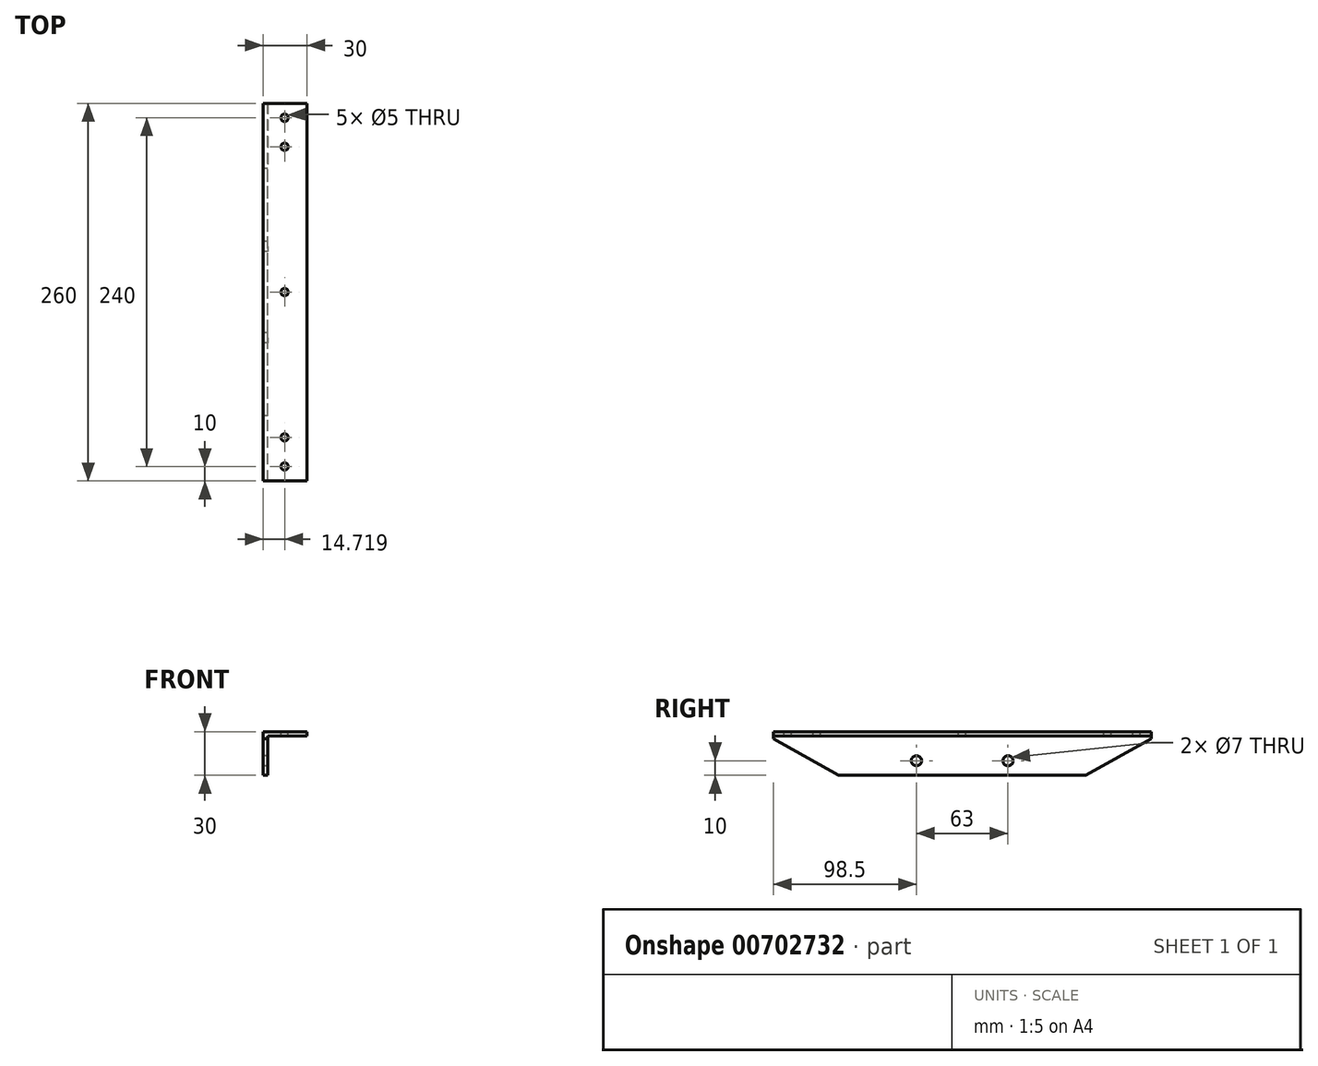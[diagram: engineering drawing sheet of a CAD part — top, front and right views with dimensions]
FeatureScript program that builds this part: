
annotation { "Feature Type Name" : "Feature", "Feature Type Description" : "" }
export const myFeature = defineFeature(function(context is Context, id is Id, definition is map)
    precondition{}
    {
        {
            var Q0;
            Q0=qCreatedBy(makeId("Front.planeOp"),FACE);
            var sketch = newSketch(context, id + "F0", { "sketchPlane" : qUnion([Q0])});
            skLineSegment(sketch, "E0", {"start": v(0, 0) * mm, "end": v(0, 30) * mm});
            skLineSegment(sketch, "E1", {"start": v(0, 30) * mm, "end": v(30, 30) * mm});
            skLineSegment(sketch, "E2", {"start": v(30, 30) * mm, "end": v(30, 27) * mm});
            skLineSegment(sketch, "E3", {"start": v(30, 27) * mm, "end": v(3, 27) * mm});
            skLineSegment(sketch, "E4", {"start": v(3, 27) * mm, "end": v(3, 0) * mm});
            skLineSegment(sketch, "E5", {"start": v(3, 0) * mm, "end": v(0, 0) * mm});
            skSolve(sketch);
        }
        {
            var Q0;
            Q0=makeQuery(id+"F0.imprint","IMPRINT",FACE,{"disambiguationData":[TD([[makeQuery(id+"F0.imprint","IMPRINT",EDGE,{"derivedFrom":sQuery(id+"F0.wireOp",EDGE,"E0")}),-1.0]])]});
            extrude(context, id + "F1", {"entities" : qUnion([Q0]), "endBound" : BoundingType.SYMMETRIC, "depth" : 260 * mm, "offsetDistance" : 25 * mm});
        }
        {
            var Q0;
            Q0=makeQuery(id+"F1.opExtrude","SWEPT_FACE",FACE,{"disambiguationData":[OSD([sQuery(id+"F0.wireOp",EDGE,"E0")])]});
            var sketch = newSketch(context, id + "F2", { "sketchPlane" : qUnion([Q0])});
            skLineSegment(sketch, "E6", {"start": v(0, 30) * mm, "end": v(0, 10) * mm});
            skLineSegment(sketch, "E7", {"start": v(0, 10) * mm, "end": v(-31.5, 10) * mm});
            skLineSegment(sketch, "E8", {"start": v(0, 10) * mm, "end": v(31.5, 10) * mm});
            skSolve(sketch);
        }
        {
            var Q0;
            Q0=sQuery(id+"F2.wireOp",VERTEX,"E7.end");
            var Q1;
            Q1=sQuery(id+"F2.wireOp",VERTEX,"E8.end");
            var Q2;
            Q2=makeQuery(id+"F1.opExtrude","SWEPT_BODY",BODY,{"disambiguationData":[OSD([sQuery(id+"F0.wireOp",EDGE,"E0"),sQuery(id+"F0.wireOp",EDGE,"E1"),sQuery(id+"F0.wireOp",EDGE,"E2"),sQuery(id+"F0.wireOp",EDGE,"E3"),sQuery(id+"F0.wireOp",EDGE,"E4"),sQuery(id+"F0.wireOp",EDGE,"E5")])]});
            hole(context, id + "F3", {"style" : HoleStyle.SIMPLE, "endStyle" : HoleEndStyle.THROUGH, "holeDiameter" : 7 * mm, "majorDiameter" : 5 * mm, "isTappedThrough" : true, "tappedDepth" : 12 * mm, "tapClearance" : 3, "locations" : qUnion([Q0, Q1]), "scope" : qUnion([Q2])});
        }
        {
            var Q0;
            Q0=makeQuery(id+"F1.opExtrude","SWEPT_FACE",FACE,{"disambiguationData":[OSD([sQuery(id+"F0.wireOp",EDGE,"E1")])]});
            var sketch = newSketch(context, id + "F4", { "sketchPlane" : qUnion([Q0])});
            skLineSegment(sketch, "E9", {"start": v(0, 0) * mm, "end": v(14.72, 0) * mm});
            skLineSegment(sketch, "E10", {"start": v(14.72, 0) * mm, "end": v(14.72, 100) * mm});
            skLineSegment(sketch, "E11", {"start": v(14.72, 0) * mm, "end": v(14.72, -100) * mm});
            skLineSegment(sketch, "E12", {"start": v(14.72, -100) * mm, "end": v(14.72, -120) * mm});
            skLineSegment(sketch, "E13", {"start": v(14.72, 100) * mm, "end": v(14.72, 120) * mm});
            skSolve(sketch);
        }
        {
            var Q0;
            Q0=sQuery(id+"F4.wireOp",VERTEX,"1tQewzAj-UfQE-Z77g-f8Yq-8VD4JALRFgvb.end");
            var Q1;
            Q1=sQuery(id+"F4.wireOp",VERTEX,"1tQewzAj-UfQE-Z77g-f8Yq-8VD4JALRFgvb.start");
            var Q2;
            Q2=sQuery(id+"F4.wireOp",VERTEX,"LTQKht7b-NH9M-FIFn-inf1-8K7WugWQLx6k.start");
            var Q3;
            Q3=sQuery(id+"F4.wireOp",VERTEX,"E11.start");
            var Q4;
            Q4=sQuery(id+"F4.wireOp",VERTEX,"Bhl9sl7J-fMcb-BVDl-VWbh-HoV6IlCvf5ou.start");
            var Q5;
            Q5=sQuery(id+"F4.wireOp",VERTEX,"l9MGoOj7-PQq2-p4TO-Y7hb-mTCIAhJtyrPD.start");
            var Q6;
            Q6=sQuery(id+"F4.wireOp",VERTEX,"l9MGoOj7-PQq2-p4TO-Y7hb-mTCIAhJtyrPD.end");
            var Q7;
            Q7=sQuery(id+"F4.wireOp",VERTEX,"gbc2nK7E-ztz0-IBhr-DfQU-EQeF7ijxsCjM.end");
            var Q8;
            Q8=sQuery(id+"F4.wireOp",VERTEX,"ZtBBAAtL-lso0-mhiq-NLzV-Yrly4486QW8c.end");
            var Q9;
            Q9=sQuery(id+"F4.wireOp",VERTEX,"SlA1qLtV-EIWa-L179-yqE0-1lIOZillnqvx.end");
            var Q10;
            Q10=sQuery(id+"F4.wireOp",VERTEX,"J0ETeXer-Zvjq-F775-bQsg-4Zvr5mP6p7do.end");
            var Q11;
            Q11=sQuery(id+"F4.wireOp",VERTEX,"E11.end");
            var Q12;
            Q12=sQuery(id+"F4.wireOp",VERTEX,"E10.end");
            var Q13;
            Q13=sQuery(id+"F4.wireOp",VERTEX,"E12.end");
            var Q14;
            Q14=sQuery(id+"F4.wireOp",VERTEX,"E13.end");
            var Q15;
            Q15=makeQuery(id+"F1.opExtrude","SWEPT_BODY",BODY,{"disambiguationData":[OSD([sQuery(id+"F0.wireOp",EDGE,"E0"),sQuery(id+"F0.wireOp",EDGE,"E1"),sQuery(id+"F0.wireOp",EDGE,"E2"),sQuery(id+"F0.wireOp",EDGE,"E3"),sQuery(id+"F0.wireOp",EDGE,"E4"),sQuery(id+"F0.wireOp",EDGE,"E5")])]});
            hole(context, id + "F5", {"style" : HoleStyle.SIMPLE, "endStyle" : HoleEndStyle.THROUGH, "holeDiameter" : 5 * mm, "majorDiameter" : 5 * mm, "isTappedThrough" : true, "tappedDepth" : 12 * mm, "tapClearance" : 3, "locations" : qUnion([Q0, Q1, Q2, Q3, Q4, Q5, Q6, Q7, Q8, Q9, Q10, Q11, Q12, Q13, Q14]), "scope" : qUnion([Q15])});
        }
        {
            var Q0;
            Q0=makeQuery(id+"F1.opExtrude","SWEPT_FACE",FACE,{"disambiguationData":[OSD([sQuery(id+"F0.wireOp",EDGE,"E0")])]});
            var sketch = newSketch(context, id + "F6", { "sketchPlane" : qUnion([Q0])});
            skLineSegment(sketch, "E14", {"start": v(-130, 25) * mm, "end": v(-130, 0) * mm});
            skLineSegment(sketch, "E15", {"start": v(-130, 0) * mm, "end": v(-85, 0) * mm});
            skLineSegment(sketch, "E16", {"start": v(-85, 0) * mm, "end": v(-130, 25) * mm});
            skLineSegment(sketch, "E17", {"start": v(130, 25) * mm, "end": v(130, 0) * mm});
            skLineSegment(sketch, "E18", {"start": v(130, 0) * mm, "end": v(85, 0) * mm});
            skLineSegment(sketch, "E19", {"start": v(85, 0) * mm, "end": v(130, 25) * mm});
            skSolve(sketch);
        }
        {
            var Q0;
            Q0=qSketchRegion(id+"F6",true);
            extrude(context, id + "F7", {"entities" : qUnion([Q0]), "operationType" : NewBodyOperationType.REMOVE, "oppositeDirection" : true, "depth" : 25 * mm, "offsetDistance" : 25 * mm});
        }
    });
